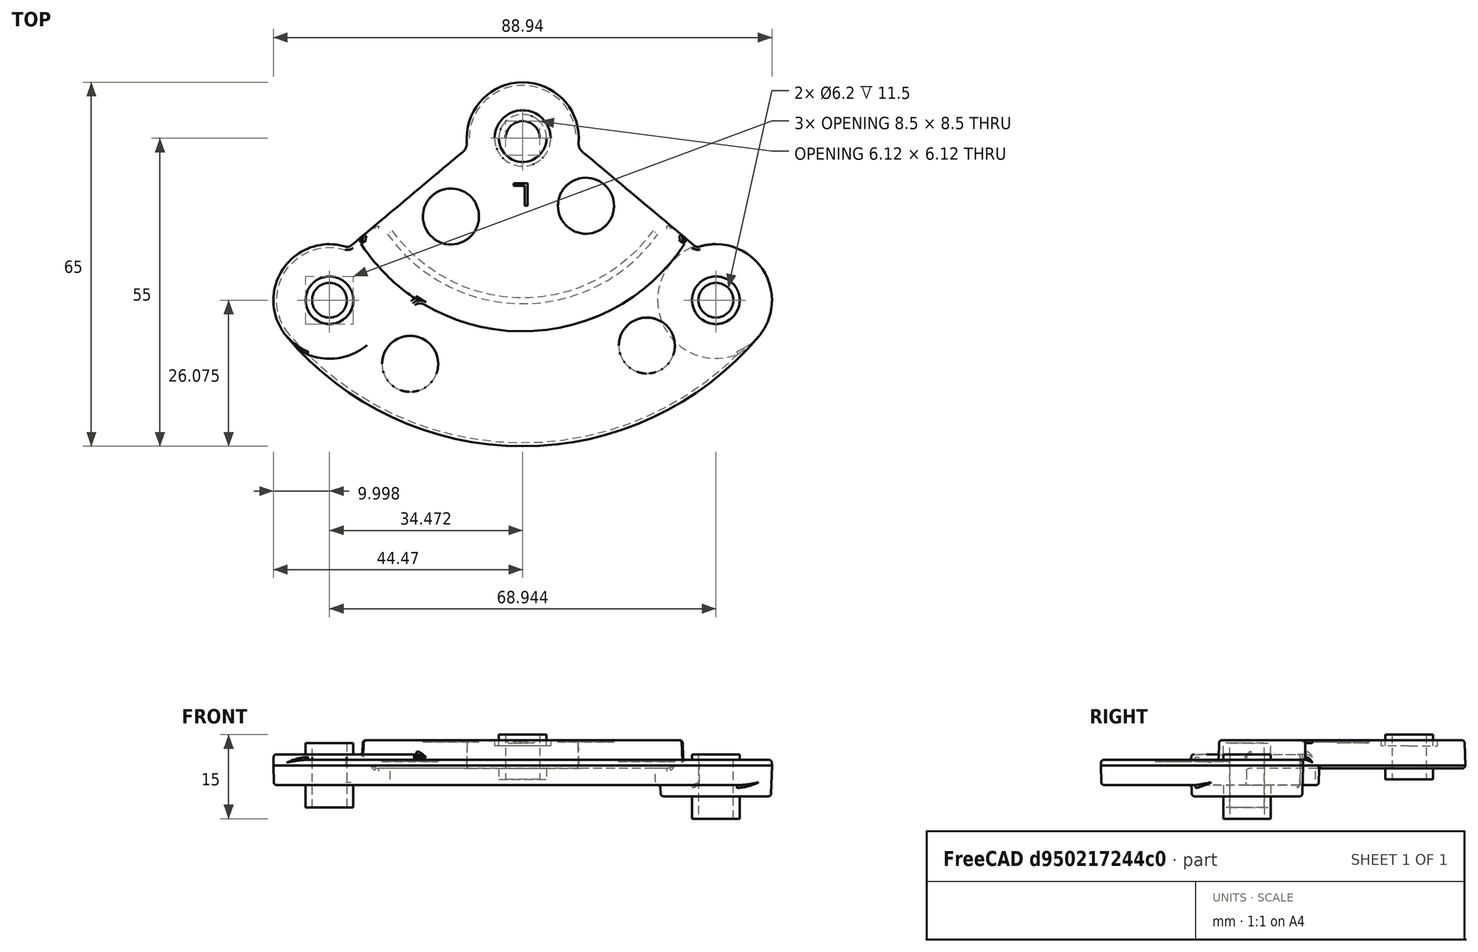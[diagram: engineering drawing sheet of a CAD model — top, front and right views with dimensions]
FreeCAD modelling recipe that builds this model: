
FCSTD DOCUMENT  (FreeCAD 0.21R33668 +26 (Git))
Label: link3_2_left
License: All rights reserved
LicenseURL: https://en.wikipedia.org/wiki/All_rights_reserved
objects: Sketcher::SketchObject×3, PartDesign::Pocket×3, Part::Feature×1, PartDesign::FeatureBase×1, PartDesign::Body×1
note: 12 computed .brp shape members not serialized (recipe doc carries the construction recipe); baked Part::Feature solids carry a one-line shape summary decoded from their .brp

FEATURE [Part::Feature] Part__Feature  label="2205006700--2021010001_12___"
  shape: bbox 95.46 x 83.6 x 15 mm, 181 faces (baked)
FEATURE [PartDesign::FeatureBase] BaseFeature
  BaseFeature = -> Part__Feature
FEATURE [Sketcher::SketchObject] Sketch
  ExternalGeometry = -> [BaseFeature]
  FullyConstrained = false
  MapMode = 5
  Placement = pos=(0,0,-10.5) rot=(0,0,1;0rad)
  Support = -> [BaseFeature]
  sketch-geometry (2):
    g0: Circle CenterX=-34.4719 CenterY=-28.9254 CenterZ=0 NormalX=0 NormalY=0 NormalZ=1 AngleXU=0 Radius=3.1
    g1: Circle CenterX=34.4721 CenterY=-28.9251 CenterZ=0 NormalX=0 NormalY=0 NormalZ=1 AngleXU=0 Radius=1.60006
  constraints (1):
    c: Diameter(g0) = 6.2
FEATURE [PartDesign::Pocket] Pocket
  BaseFeature = -> BaseFeature
  Direction = (0,0,-1)
  Length = 5
  Length2 = 5
  Profile = -> Sketch
  ReferenceAxis = -> Sketch [N_Axis]
  Type = 1
FEATURE [Sketcher::SketchObject] Sketch002
  FullyConstrained = false
  MapMode = 5
  Placement = pos=(0,0,-24) rot=(1,0,0;3.14159rad)
  sketch-geometry (1):
    g0: Circle CenterX=34.472 CenterY=28.9254 CenterZ=0 NormalX=0 NormalY=0 NormalZ=1 AngleXU=0 Radius=3.1
  constraints (1):
    c: Diameter(g0) = 6.2
FEATURE [PartDesign::Pocket] Pocket002
  BaseFeature = -> Pocket
  Direction = (0,0,1)
  Length = 5
  Length2 = 5
  Profile = -> Sketch002
  ReferenceAxis = -> Sketch002 [N_Axis]
  Type = 1
FEATURE [Sketcher::SketchObject] Sketch003
  ExternalGeometry = -> [Pocket002]
  FullyConstrained = true
  MapMode = 5
  Placement = pos=(0,0,-24) rot=(1,0,0;3.14159rad)
  Support = -> [Pocket002]
  sketch-geometry (1):
    g0: Circle CenterX=34.472 CenterY=28.9254 CenterZ=0 NormalX=0 NormalY=0 NormalZ=1 AngleXU=0 Radius=3.1
  constraints (2):
    c: Coincident(g0,g-3)
    c: Diameter(g0) = 6.2
FEATURE [PartDesign::Pocket] Pocket003
  BaseFeature = -> Pocket002
  Direction = (0,0,1)
  Length = 5
  Length2 = 5
  Profile = -> Sketch003
  ReferenceAxis = -> Sketch003 [N_Axis]
  Type = 1
FEATURE [PartDesign::Body] Body
  BaseFeature = -> Part__Feature
  Group = -> [BaseFeature,Sketch,Pocket,Sketch002,Pocket002,Sketch003,Pocket003]
  Origin = -> Origin
  Tip = -> Pocket003
